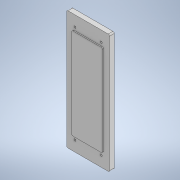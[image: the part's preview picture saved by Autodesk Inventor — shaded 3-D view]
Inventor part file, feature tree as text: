
AUTODESK INVENTOR PART (.ipt)
format: ipt  version: 2021 (Build 250183000, 183)  size: 131,072 bytes
history: native  units: mm
features: extrude x3, sketch x3, fillet x1
ambient origin geometry x8: Origin, YZ Plane, XZ Plane, XY Plane, X Axis, Y Axis, Z Axis, Center Point
bodies: Solid1 (feature_tree)
feature tree (7):
  extrude  "Extrusion1"  Depth=186.0mm
  extrude  "Extrusion2"  Depth=48.0mm
  fillet  "Fillet1"  Radius=142.6mm
  extrude  "Extrusion3"  Depth=2.0mm
  sketch  "Sketch1"  dims[d0=67.0mm d1=186.0mm]
  sketch  "Sketch2"  dims[d2=7.4mm d3=0.0mm d4=48.0mm d5=142.6mm]
  sketch  "Sketch3"  dims[d6=1.6mm d7=0.0mm d8=2.0mm d9=3.0mm d10=41.0mm d11=153.0mm d12=0.0mm d13=0.0mm]
